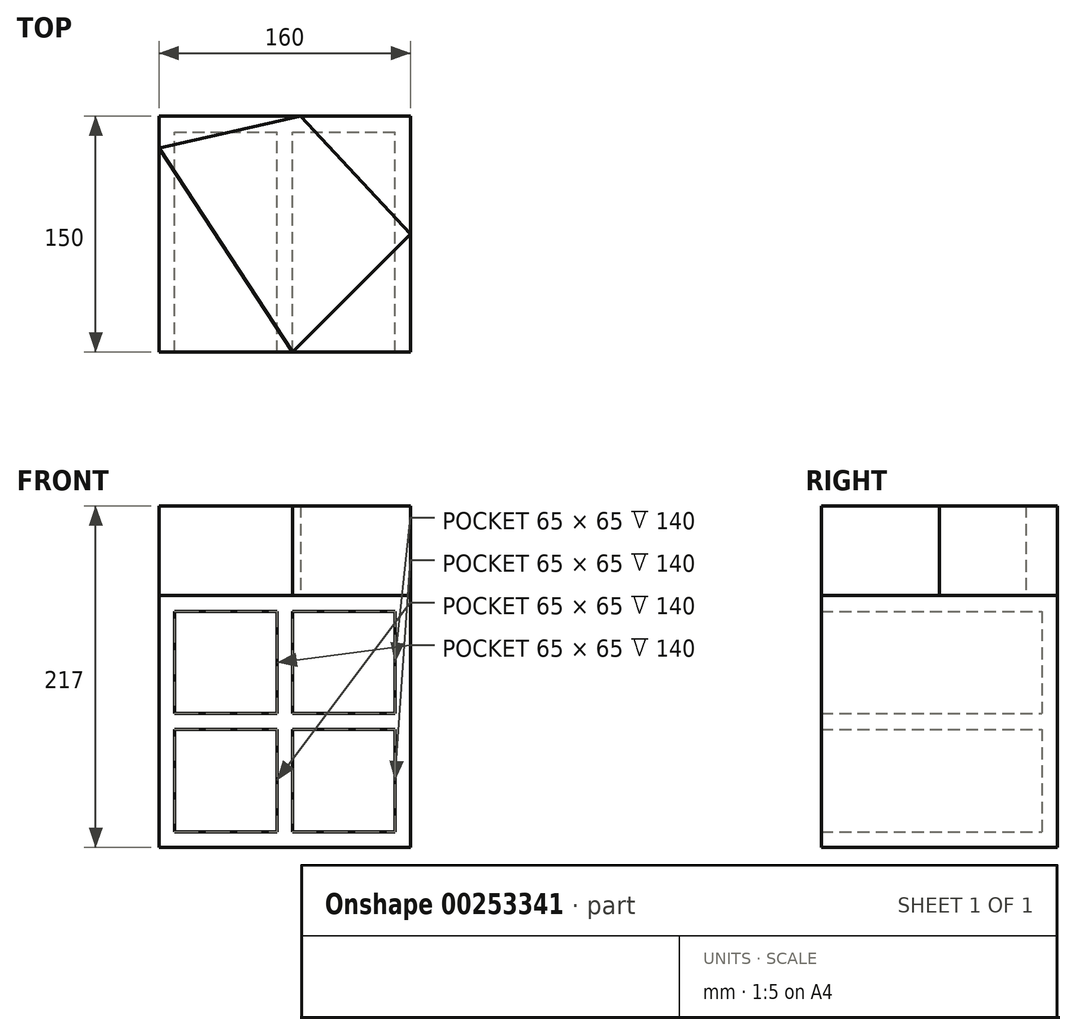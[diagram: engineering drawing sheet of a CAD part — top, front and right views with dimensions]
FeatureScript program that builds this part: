
annotation { "Feature Type Name" : "Feature", "Feature Type Description" : "" }
export const myFeature = defineFeature(function(context is Context, id is Id, definition is map)
    precondition{}
    {
        {
            var Q0;
            Q0=qCreatedBy(makeId("Front.planeOp"),FACE);
            var sketch = newSketch(context, id + "F0", { "sketchPlane" : qUnion([Q0])});
            skLineSegment(sketch, "E0.bottom", {"start": v(-191.56, 130.33) * mm, "end": v(-31.56, 130.33) * mm});
            skLineSegment(sketch, "E0.top", {"start": v(-191.56, -29.67) * mm, "end": v(-31.56, -29.67) * mm});
            skLineSegment(sketch, "E0.left", {"start": v(-191.56, 130.33) * mm, "end": v(-191.56, -29.67) * mm});
            skLineSegment(sketch, "E0.right", {"start": v(-31.56, 130.33) * mm, "end": v(-31.56, -29.67) * mm});
            skLineSegment(sketch, "E1.0", {"start": v(-181.56, 120.33) * mm, "end": v(-41.56, 120.33) * mm});
            skLineSegment(sketch, "E1.1", {"start": v(-181.56, 120.33) * mm, "end": v(-181.56, -19.67) * mm});
            skLineSegment(sketch, "E1.2", {"start": v(-181.56, -19.67) * mm, "end": v(-41.56, -19.67) * mm});
            skLineSegment(sketch, "E1.3", {"start": v(-41.56, 120.33) * mm, "end": v(-41.56, -19.67) * mm});
            skLineSegment(sketch, "E2", {"start": v(-116.56, 120.33) * mm, "end": v(-116.56, -19.67) * mm});
            skLineSegment(sketch, "E3", {"start": v(-106.56, 120.33) * mm, "end": v(-106.56, -19.67) * mm});
            skLineSegment(sketch, "E4", {"start": v(-181.56, 55.33) * mm, "end": v(-41.56, 55.33) * mm});
            skLineSegment(sketch, "E5", {"start": v(-181.56, 45.33) * mm, "end": v(-41.56, 45.33) * mm});
            skSolve(sketch);
        }
        {
            var Q0;
            Q0=makeQuery(id+"F0.imprint","IMPRINT",FACE,{"disambiguationData":[TD([[makeQuery(id+"F0.imprint","IMPRINT",EDGE,{"derivedFrom":sQuery(id+"F0.wireOp",EDGE,"E0.bottom")}),-1.0]])]});
            var Q1;
            {var subQ0=sQuery(id+"F0.wireOp",EDGE,"E4");var subQ1=sQuery(id+"F0.wireOp",EDGE,"E1.1");var subQ2=makeQuery(id+"F0.imprint","INTERSECT",VERTEX,{"derivedFrom":[subQ1,subQ0]});Q1=makeQuery(id+"F0.imprint","IMPRINT",FACE,{"disambiguationData":[TD([[makeQuery(id+"F0.imprint","IMPRINT",EDGE,{"disambiguationData":[TD([[subQ2,-1.0]])],"derivedFrom":subQ1}),1.0]])]});}
            var Q2;
            {var subQ0=sQuery(id+"F0.wireOp",EDGE,"E2");var subQ1=sQuery(id+"F0.wireOp",EDGE,"E1.0");var subQ2=makeQuery(id+"F0.imprint","INTERSECT",VERTEX,{"derivedFrom":[subQ1,subQ0]});Q2=makeQuery(id+"F0.imprint","IMPRINT",FACE,{"disambiguationData":[TD([[makeQuery(id+"F0.imprint","IMPRINT",EDGE,{"disambiguationData":[TD([[subQ2,-1.0]])],"derivedFrom":subQ1}),-1.0]])]});}
            var Q3;
            {var subQ0=sQuery(id+"F0.wireOp",EDGE,"E4");var subQ1=sQuery(id+"F0.wireOp",EDGE,"E1.3");var subQ2=makeQuery(id+"F0.imprint","INTERSECT",VERTEX,{"derivedFrom":[subQ1,subQ0]});Q3=makeQuery(id+"F0.imprint","IMPRINT",FACE,{"disambiguationData":[TD([[makeQuery(id+"F0.imprint","IMPRINT",EDGE,{"disambiguationData":[TD([[subQ2,-1.0]])],"derivedFrom":subQ1}),-1.0]])]});}
            var Q4;
            {var subQ0=sQuery(id+"F0.wireOp",EDGE,"E2");var subQ1=sQuery(id+"F0.wireOp",EDGE,"E1.2");var subQ2=makeQuery(id+"F0.imprint","INTERSECT",VERTEX,{"derivedFrom":[subQ1,subQ0]});Q4=makeQuery(id+"F0.imprint","IMPRINT",FACE,{"disambiguationData":[TD([[makeQuery(id+"F0.imprint","IMPRINT",EDGE,{"disambiguationData":[TD([[subQ2,-1.0]])],"derivedFrom":subQ1}),1.0]])]});}
            var Q5;
            {var subQ0=sQuery(id+"F0.wireOp",EDGE,"E4");var subQ1=sQuery(id+"F0.wireOp",EDGE,"E2");var subQ2=makeQuery(id+"F0.imprint","INTERSECT",VERTEX,{"derivedFrom":[subQ1,subQ0]});Q5=makeQuery(id+"F0.imprint","IMPRINT",FACE,{"disambiguationData":[TD([[makeQuery(id+"F0.imprint","IMPRINT",EDGE,{"disambiguationData":[TD([[subQ2,-1.0]])],"derivedFrom":subQ1}),1.0]])]});}
            extrude(context, id + "F1", {"entities" : qUnion([Q0, Q1, Q2, Q3, Q4, Q5]), "depth" : 150 * mm});
        }
        {
            var Q0;
            Q0=makeQuery(id+"F1.opExtrude","SWEPT_FACE",FACE,{"disambiguationData":[OSD([sQuery(id+"F0.wireOp",EDGE,"E0.right")])]});
            var sketch = newSketch(context, id + "F2", { "sketchPlane" : qUnion([Q0])});
            skLineSegment(sketch, "E6", {"start": v(-10, 130.33) * mm, "end": v(-10, -29.67) * mm});
            skSolve(sketch);
        }
        {
            var Q0;
            Q0 = qSketchRegion(id + "F2", true);
            var Q1;
            {var subQ0=sQuery(id+"F2.wireOp",EDGE,"E6");Q1=makeQuery(id+"F2.imprint","IMPRINT",FACE,{"disambiguationData":[TD([[makeQuery(id+"F2.imprint","IMPRINT",EDGE,{"derivedFrom":subQ0}),1.0]])]});}
            extrude(context, id + "F3", {"entities" : qUnion([Q0, Q1]), "operationType" : NewBodyOperationType.ADD, "oppositeDirection" : true, "depth" : 150 * mm});
        }
        {
            var Q0;
            Q0=makeQuery(id+"F1.opExtrude","SWEPT_FACE",FACE,{"disambiguationData":[OSD([sQuery(id+"F0.wireOp",EDGE,"E0.bottom")])]});
            var sketch = newSketch(context, id + "F4", { "sketchPlane" : qUnion([Q0])});
            skLineSegment(sketch, "E7", {"start": v(-191.56, -20.16) * mm, "end": v(-106.56, -150) * mm});
            skLineSegment(sketch, "E8", {"start": v(-106.56, -150) * mm, "end": v(-31.56, -75) * mm});
            skLineSegment(sketch, "E9", {"start": v(-31.56, -75) * mm, "end": v(-101.4, 0) * mm});
            skLineSegment(sketch, "E10", {"start": v(-101.4, 0) * mm, "end": v(-191.56, -20.16) * mm});
            skSolve(sketch);
        }
        {
            var Q0;
            Q0 = qSketchRegion(id + "F4", true);
            extrude(context, id + "F5", {"entities" : qUnion([Q0]), "operationType" : NewBodyOperationType.ADD, "depth" : 57 * mm});
        }
    });
